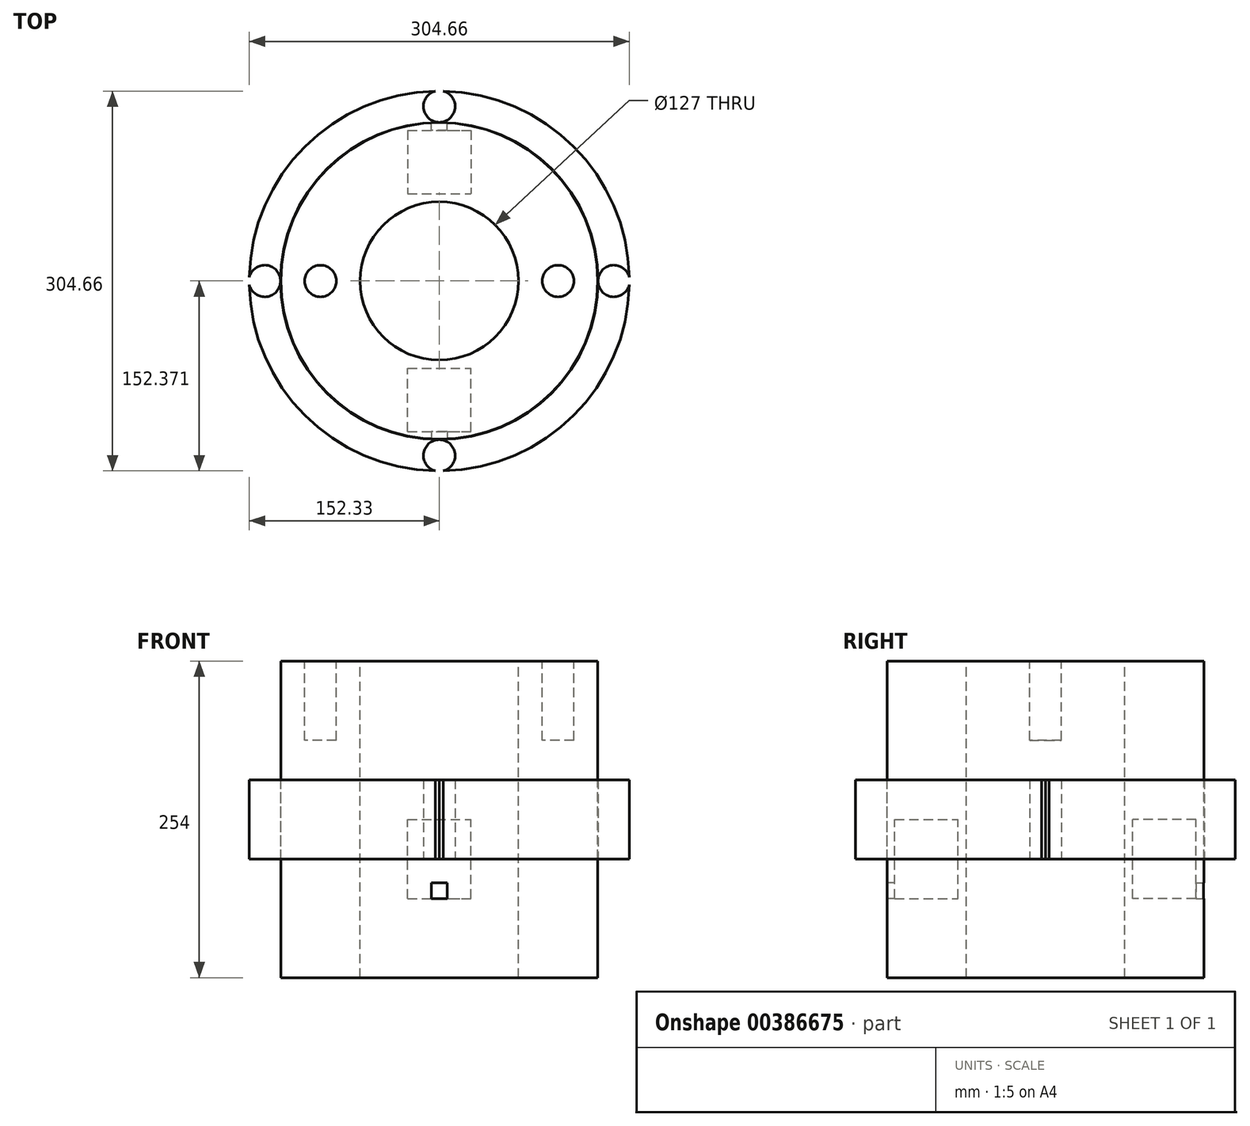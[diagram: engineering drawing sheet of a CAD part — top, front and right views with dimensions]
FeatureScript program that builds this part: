
annotation { "Feature Type Name" : "Feature", "Feature Type Description" : "" }
export const myFeature = defineFeature(function(context is Context, id is Id, definition is map)
    precondition{}
    {
        {
            var Q0;
            Q0=qCreatedBy(makeId("Top.planeOp"),FACE);
            var sketch = newSketch(context, id + "F0", { "sketchPlane" : qUnion([Q0])});
            skCircle(sketch, "E0", {"center": v(0, 0.04) * mm, "radius": 63.5 * mm});
            skCircle(sketch, "E1.0", {"center": v(0, 0.04) * mm, "radius": 127 * mm});
            skSolve(sketch);
        }
        {
            var Q0;
            Q0=makeQuery(id+"F0.imprint","IMPRINT",FACE,{"disambiguationData":[TD([[makeQuery(id+"F0.imprint","IMPRINT",EDGE,{"derivedFrom":sQuery(id+"F0.wireOp",EDGE,"E0")}),-1.0]])]});
            extrude(context, id + "F1", {"entities" : qUnion([Q0]), "endBound" : BoundingType.SYMMETRIC, "oppositeDirection" : true, "depth" : 254 * mm});
        }
        {
            var Q0;
            Q0=qCreatedBy(makeId("Top.planeOp"),FACE);
            var sketch = newSketch(context, id + "F2", { "sketchPlane" : qUnion([Q0])});
            skCircle(sketch, "E2", {"center": v(0, 0) * mm, "radius": 152.36 * mm});
            skCircle(sketch, "E3", {"center": v(0, 0) * mm, "radius": 127.3 * mm});
            skSolve(sketch);
        }
        {
            var Q0;
            Q0 = qSketchRegion(id + "F2", true);
            extrude(context, id + "F3", {"entities" : qUnion([Q0]), "endBound" : BoundingType.SYMMETRIC, "depth" : 63.5 * mm});
        }
        {
            var Q0;
            Q0=makeQuery(id+"F3.opExtrude","CAP_FACE",FACE,{"disambiguationData":[OSD([sQuery(id+"F2.wireOp",EDGE,"E2"),sQuery(id+"F2.wireOp",EDGE,"E3")])],"isStart":true});
            var sketch = newSketch(context, id + "F4", { "sketchPlane" : qUnion([Q0])});
            skCircle(sketch, "E4", {"center": v(140, 0) * mm, "radius": 12.7 * mm});
            skCircle(sketch, "E5.1.0", {"center": v(0, -140) * mm, "radius": 12.7 * mm});
            skCircle(sketch, "E5.2.0", {"center": v(-140, 0) * mm, "radius": 12.7 * mm});
            skPoint(sketch, "E5.center", {"position": v(0, 0) * mm});
            skLineSegment(sketch, "E5.anchor1", {"start": v(0, 0) * mm, "end": v(140, 0) * mm, "construction": true});
            skLineSegment(sketch, "E5.anchor2", {"start": v(0, 0) * mm, "end": v(-140, 0) * mm, "construction": true});
            skCircle(sketch, "E6.2.0", {"center": v(0, 140) * mm, "radius": 12.7 * mm});
            skLineSegment(sketch, "E6.anchor2", {"start": v(0, 0) * mm, "end": v(0, 140) * mm, "construction": true});
            skSolve(sketch);
        }
        {
            var Q0;
            Q0 = qSketchRegion(id + "F4", true);
            extrude(context, id + "F5", {"entities" : qUnion([Q0]), "operationType" : NewBodyOperationType.REMOVE, "endBound" : BoundingType.THROUGH_ALL, "oppositeDirection" : true, "depth" : 25.4 * mm});
        }
        {
            var Q0;
            Q0=makeQuery(id+"F1.opExtrude","CAP_FACE",FACE,{"disambiguationData":[OSD([sQuery(id+"F0.wireOp",EDGE,"E0"),sQuery(id+"F0.wireOp",EDGE,"E1.0")])],"isStart":true});
            var sketch = newSketch(context, id + "F6", { "sketchPlane" : qUnion([Q0])});
            skCircle(sketch, "E7", {"center": v(-95.25, 0) * mm, "radius": 12.7 * mm});
            skCircle(sketch, "E8.2.0", {"center": v(95.25, 0) * mm, "radius": 12.7 * mm});
            skPoint(sketch, "E8.center", {"position": v(0, 0) * mm});
            skLineSegment(sketch, "E8.anchor1", {"start": v(0, 0) * mm, "end": v(-95.25, 0) * mm, "construction": true});
            skLineSegment(sketch, "E8.anchor2", {"start": v(0, 0) * mm, "end": v(95.25, 0) * mm, "construction": true});
            skSolve(sketch);
        }
        {
            var Q0;
            Q0 = qSketchRegion(id + "F6", true);
            extrude(context, id + "F7", {"entities" : qUnion([Q0]), "operationType" : NewBodyOperationType.REMOVE, "oppositeDirection" : true, "depth" : 63.5 * mm});
        }
        {
            var Q0;
            Q0=qCreatedBy(makeId("Top.planeOp"),FACE);
            var sketch = newSketch(context, id + "F8", { "sketchPlane" : qUnion([Q0])});
            skLineSegment(sketch, "E9.bottom", {"start": v(-25.4, 120.7) * mm, "end": v(25.4, 120.7) * mm});
            skLineSegment(sketch, "E9.top", {"start": v(-25.4, 69.9) * mm, "end": v(25.4, 69.9) * mm});
            skLineSegment(sketch, "E9.left", {"start": v(-25.4, 120.7) * mm, "end": v(-25.4, 69.9) * mm});
            skLineSegment(sketch, "E9.right", {"start": v(25.4, 120.7) * mm, "end": v(25.4, 69.9) * mm});
            skPoint(sketch, "E10.middle", {"position": v(0, 120.7) * mm});
            skLineSegment(sketch, "E11", {"start": v(-58.93, 0) * mm, "end": v(55.88, 0) * mm});
            skLineSegment(sketch, "E12.MirrorCS", {"start": v(-25.4, -69.9) * mm, "end": v(25.4, -69.9) * mm});
            skLineSegment(sketch, "E13.MirrorCS", {"start": v(-25.4, -120.7) * mm, "end": v(-25.4, -69.9) * mm});
            skLineSegment(sketch, "E14.MirrorCS", {"start": v(25.4, -120.7) * mm, "end": v(25.4, -69.9) * mm});
            skLineSegment(sketch, "E15.MirrorCS", {"start": v(-25.4, -120.7) * mm, "end": v(25.4, -120.7) * mm});
            skSolve(sketch);
        }
        {
            var Q0;
            Q0 = qSketchRegion(id + "F8", true);
            extrude(context, id + "F9", {"entities" : qUnion([Q0]), "operationType" : NewBodyOperationType.REMOVE, "oppositeDirection" : true, "depth" : 63.5 * mm});
        }
        {
            var Q0;
            Q0=qCreatedBy(makeId("Top.planeOp"),FACE);
            cPlane(context, id + "F10", {"entities" : qUnion([Q0]), "cplaneType" : CPlaneType.OFFSET, "offset" : 63.5 * mm, "oppositeDirection" : true, "width" : 152.4 * mm, "height" : 152.4 * mm});
        }
        {
            var Q0;
            Q0=qCreatedBy(id+"F10.planeOp",FACE);
            var sketch = newSketch(context, id + "F11", { "sketchPlane" : qUnion([Q0])});
            skLineSegment(sketch, "E16.bottom", {"start": v(-6.35, 114.34) * mm, "end": v(6.35, 114.34) * mm});
            skLineSegment(sketch, "E16.top", {"start": v(-6.35, 139.74) * mm, "end": v(6.35, 139.74) * mm});
            skLineSegment(sketch, "E16.left", {"start": v(-6.35, 114.34) * mm, "end": v(-6.35, 139.74) * mm});
            skLineSegment(sketch, "E16.right", {"start": v(6.35, 114.34) * mm, "end": v(6.35, 139.74) * mm});
            skPoint(sketch, "E16.middle", {"position": v(0, 127.04) * mm});
            skLineSegment(sketch, "E17", {"start": v(-59.44, 0) * mm, "end": v(55.37, 0) * mm});
            skLineSegment(sketch, "E18.MirrorCS", {"start": v(-6.35, -114.34) * mm, "end": v(6.35, -114.34) * mm});
            skLineSegment(sketch, "E19.MirrorCS", {"start": v(-6.35, -114.34) * mm, "end": v(-6.35, -139.74) * mm});
            skLineSegment(sketch, "E20.MirrorCS", {"start": v(6.35, -114.34) * mm, "end": v(6.35, -139.74) * mm});
            skLineSegment(sketch, "E21.MirrorCS", {"start": v(-6.35, -139.74) * mm, "end": v(6.35, -139.74) * mm});
            skSolve(sketch);
        }
        {
            var Q0;
            Q0 = qSketchRegion(id + "F11", true);
            extrude(context, id + "F12", {"entities" : qUnion([Q0]), "operationType" : NewBodyOperationType.REMOVE, "depth" : 12.7 * mm});
        }
    });
